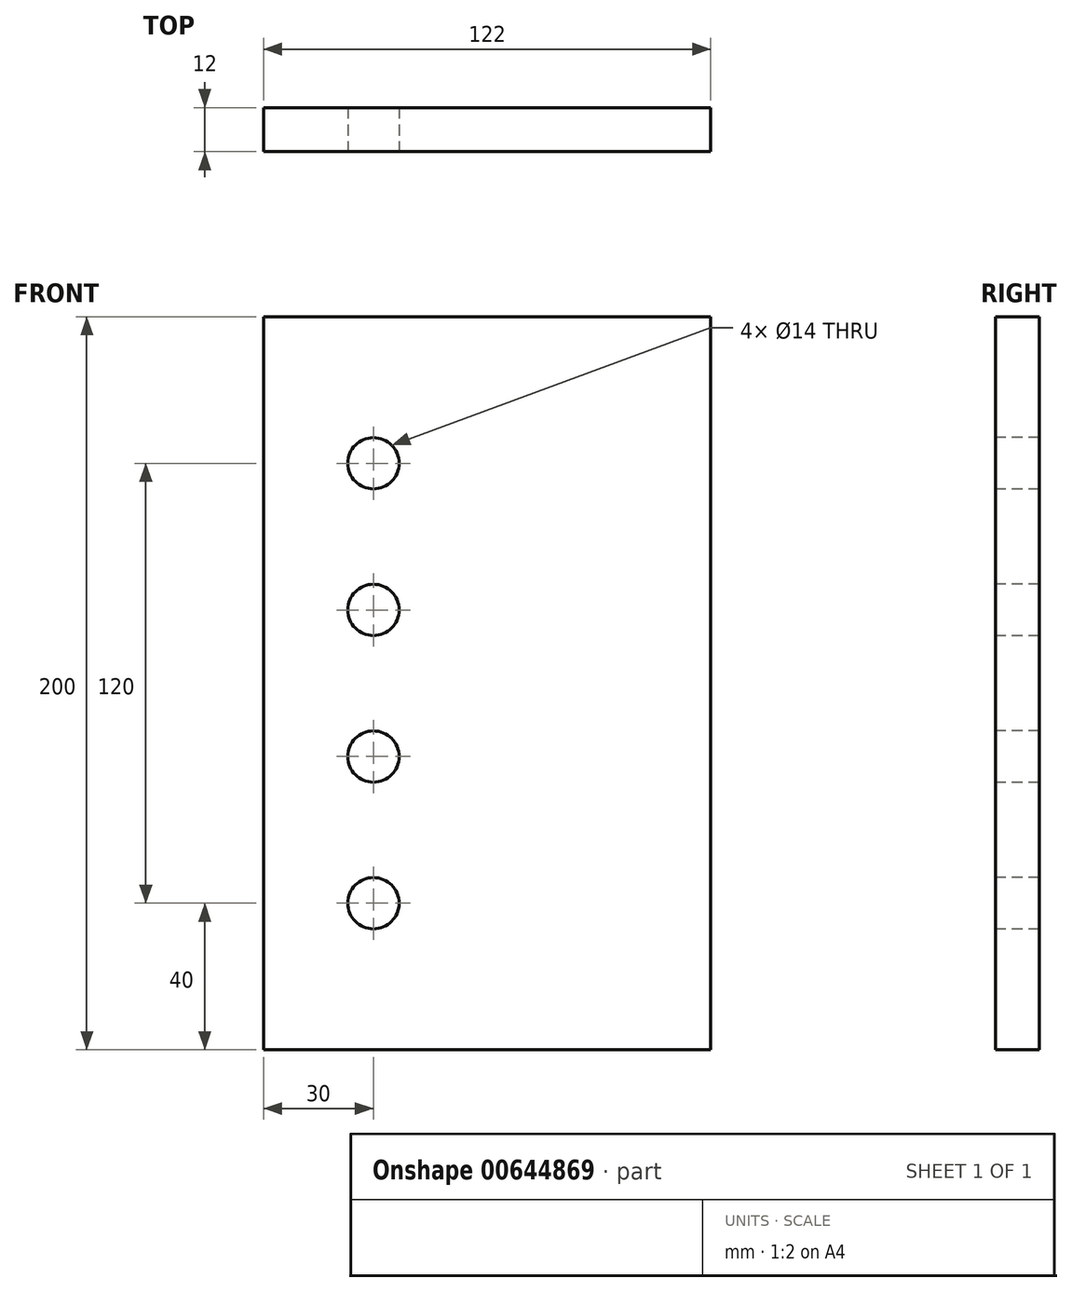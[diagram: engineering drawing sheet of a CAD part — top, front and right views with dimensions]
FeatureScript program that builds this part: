
annotation { "Feature Type Name" : "Feature", "Feature Type Description" : "" }
export const myFeature = defineFeature(function(context is Context, id is Id, definition is map)
    precondition{}
    {
        {
            var Q0;
            Q0=qCreatedBy(makeId("Front.planeOp"),FACE);
            var sketch = newSketch(context, id + "F0", { "sketchPlane" : qUnion([Q0])});
            skLineSegment(sketch, "E0.bottom", {"start": v(0, 0) * mm, "end": v(122, 0) * mm});
            skLineSegment(sketch, "E0.top", {"start": v(0, 200) * mm, "end": v(122, 200) * mm});
            skLineSegment(sketch, "E0.left", {"start": v(0, 0) * mm, "end": v(0, 200) * mm});
            skLineSegment(sketch, "E0.right", {"start": v(122, 0) * mm, "end": v(122, 200) * mm});
            skSolve(sketch);
        }
        {
            var Q0;
            Q0=makeQuery(id+"F0.imprint","IMPRINT",FACE,{"disambiguationData":[TD([[makeQuery(id+"F0.imprint","IMPRINT",EDGE,{"derivedFrom":sQuery(id+"F0.wireOp",EDGE,"E0.bottom")}),1.0]])]});
            extrude(context, id + "F1", {"entities" : qUnion([Q0]), "depth" : 12 * mm});
        }
        {
            var Q0;
            Q0=makeQuery(id+"F1.opExtrude","CAP_FACE",FACE,{"disambiguationData":[OSD([sQuery(id+"F0.wireOp",EDGE,"E0.bottom"),sQuery(id+"F0.wireOp",EDGE,"E0.top"),sQuery(id+"F0.wireOp",EDGE,"E0.left"),sQuery(id+"F0.wireOp",EDGE,"E0.right")])],"isStart":false});
            var sketch = newSketch(context, id + "F2", { "sketchPlane" : qUnion([Q0])});
            skPoint(sketch, "E1", {"position": v(30, 160) * mm});
            skPoint(sketch, "E2", {"position": v(30, 120) * mm});
            skPoint(sketch, "E3", {"position": v(30, 80) * mm});
            skPoint(sketch, "E4", {"position": v(30, 40) * mm});
            skSolve(sketch);
        }
        {
            var Q0;
            Q0=sQuery(id+"F2.wireOp",VERTEX,"E1");
            var Q1;
            Q1=sQuery(id+"F2.wireOp",VERTEX,"E2");
            var Q2;
            Q2=sQuery(id+"F2.wireOp",VERTEX,"E3");
            var Q3;
            Q3=sQuery(id+"F2.wireOp",VERTEX,"E4");
            var Q4;
            Q4=makeQuery(id+"F1.opExtrude","SWEPT_BODY",BODY,{"disambiguationData":[OSD([sQuery(id+"F0.wireOp",EDGE,"E0.bottom"),sQuery(id+"F0.wireOp",EDGE,"E0.top"),sQuery(id+"F0.wireOp",EDGE,"E0.left"),sQuery(id+"F0.wireOp",EDGE,"E0.right")])]});
            hole(context, id + "F3", {"style" : HoleStyle.SIMPLE, "endStyle" : HoleEndStyle.THROUGH, "holeDiameter" : 14 * mm, "tappedDepth" : 12 * mm, "tapClearance" : 3, "locations" : qUnion([Q0, Q1, Q2, Q3]), "scope" : qUnion([Q4])});
        }
    });
